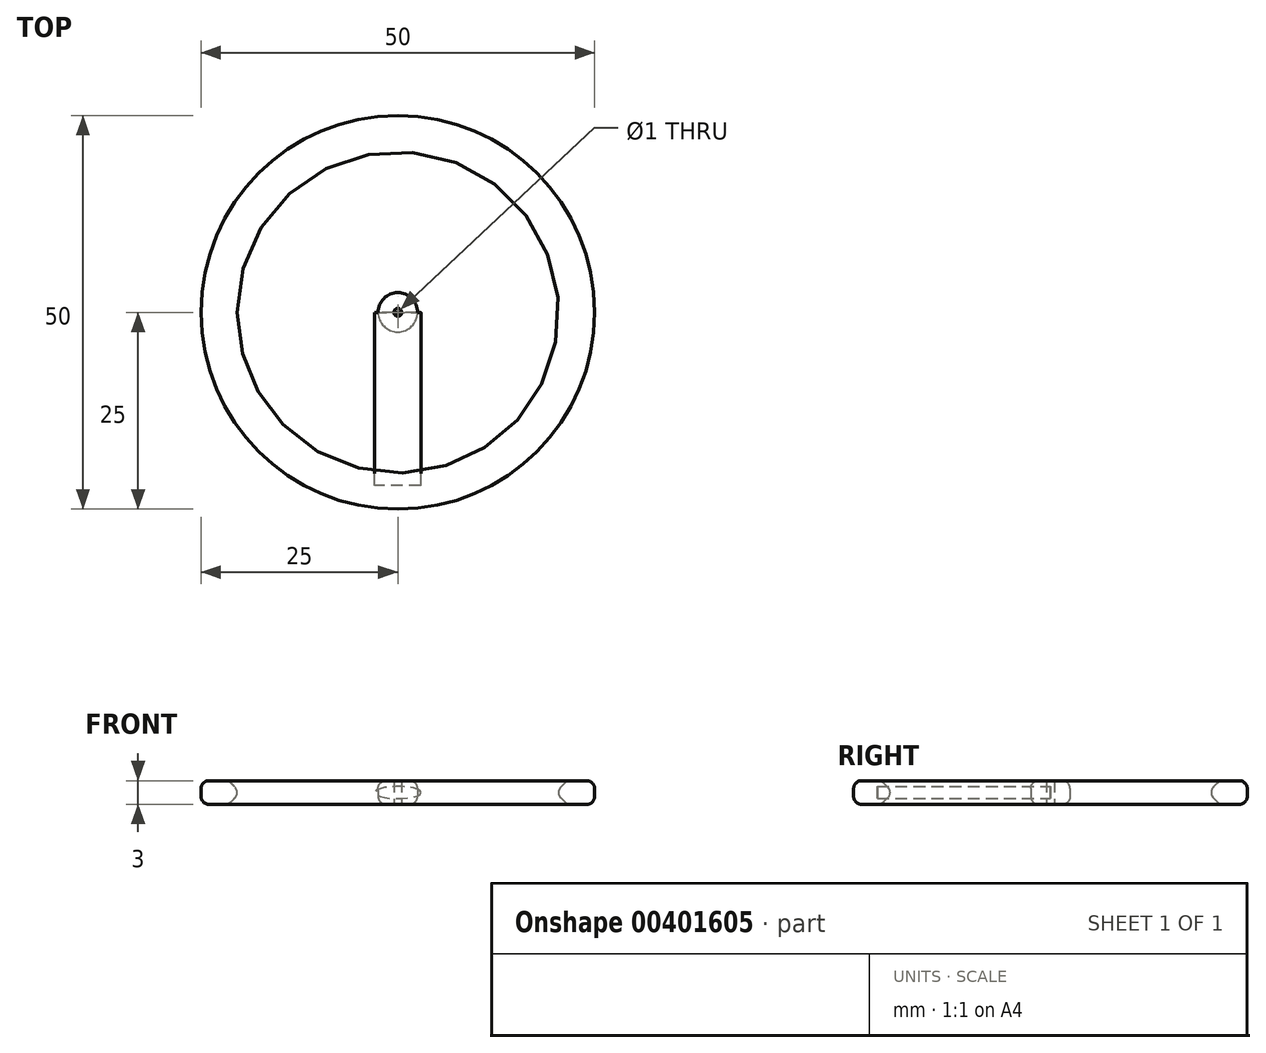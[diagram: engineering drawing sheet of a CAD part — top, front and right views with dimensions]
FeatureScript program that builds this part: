
annotation { "Feature Type Name" : "Feature", "Feature Type Description" : "" }
export const myFeature = defineFeature(function(context is Context, id is Id, definition is map)
    precondition{}
    {
        {
            var Q0;
            Q0=qCreatedBy(makeId("Top.planeOp"),FACE);
            var sketch = newSketch(context, id + "F0", { "sketchPlane" : qUnion([Q0])});
            skCircle(sketch, "E0", {"center": v(0, 0) * mm, "radius": 25 * mm});
            skCircle(sketch, "E1", {"center": v(0, 0) * mm, "radius": 20 * mm});
            skCircle(sketch, "E2", {"center": v(0, 0) * mm, "radius": 2.5 * mm});
            skCircle(sketch, "E3", {"center": v(0, 0) * mm, "radius": 0.5 * mm});
            skSolve(sketch);
        }
        {
            var Q0;
            Q0=makeQuery(id+"F0.imprint","IMPRINT",FACE,{"disambiguationData":[TD([[makeQuery(id+"F0.imprint","IMPRINT",EDGE,{"derivedFrom":sQuery(id+"F0.wireOp",EDGE,"E2")}),1.0]])]});
            var Q1;
            Q1=makeQuery(id+"F0.imprint","IMPRINT",FACE,{"disambiguationData":[TD([[makeQuery(id+"F0.imprint","IMPRINT",EDGE,{"derivedFrom":sQuery(id+"F0.wireOp",EDGE,"E0")}),1.0]])]});
            extrude(context, id + "F1", {"entities" : qUnion([Q0, Q1]), "endBound" : BoundingType.SYMMETRIC, "depth" : 3 * mm});
        }
        {
            var Q0;
            Q0=qCreatedBy(makeId("Front.planeOp"),FACE);
            var sketch = newSketch(context, id + "F2", { "sketchPlane" : qUnion([Q0])});
            skEllipse(sketch, "E4", {"center": v(0, 0) * mm, "majorRadius": 2.93 * mm, "minorRadius": 0.77 * mm, "majorAxis": v(1, 0)});
            skSolve(sketch);
        }
        {
            var Q0;
            Q0 = qSketchRegion(id + "F2", true);
            extrude(context, id + "F3", {"entities" : qUnion([Q0]), "depth" : 22 * mm});
        }
        {
            var Q0;
            Q0=makeQuery(id+"F1.opExtrude","CAP_EDGE",EDGE,{"disambiguationData":[OSD([sQuery(id+"F0.wireOp",EDGE,"E1")])],"isStart":false});
            var Q1;
            Q1=makeQuery(id+"F1.opExtrude","CAP_EDGE",EDGE,{"disambiguationData":[OSD([sQuery(id+"F0.wireOp",EDGE,"E1")])],"isStart":true});
            chamfer(context, id + "F4", {"entities" : qUnion([Q0, Q1]), "width" : 1.5 * mm, "tangentPropagation" : true});
        }
        {
            var Q0;
            {var subQ0=sQuery(id+"F0.wireOp",EDGE,"E1");Q0=makeQuery(id+"F4.opChamfer","BLEND_EDGE",EDGE,{"blendedFrom":[makeQuery(id+"F1.opExtrude","CAP_EDGE",EDGE,{"disambiguationData":[OSD([subQ0])],"isStart":false}),makeQuery(id+"F1.opExtrude","CAP_FACE",FACE,{"disambiguationData":[OSD([sQuery(id+"F0.wireOp",EDGE,"E0"),subQ0])],"isStart":false})],"blendedInto":[makeQuery(id+"F1.opExtrude","CAP_FACE",FACE,{"disambiguationData":[OSD([sQuery(id+"F0.wireOp",EDGE,"E0"),subQ0])],"isStart":false})]});}
            var Q1;
            {var subQ0=sQuery(id+"F0.wireOp",EDGE,"E1");Q1=makeQuery(id+"F4.opChamfer","BLEND_EDGE",EDGE,{"blendedFrom":[makeQuery(id+"F1.opExtrude","CAP_EDGE",EDGE,{"disambiguationData":[OSD([subQ0])],"isStart":true}),makeQuery(id+"F1.opExtrude","CAP_FACE",FACE,{"disambiguationData":[OSD([sQuery(id+"F0.wireOp",EDGE,"E0"),subQ0])],"isStart":true})],"blendedInto":[makeQuery(id+"F1.opExtrude","CAP_FACE",FACE,{"disambiguationData":[OSD([sQuery(id+"F0.wireOp",EDGE,"E0"),subQ0])],"isStart":true})]});}
            var Q2;
            {var subQ0=sQuery(id+"F0.wireOp",EDGE,"E1");Q2=makeQuery(id+"F4.opChamfer","BLEND_EDGE",EDGE,{"blendedFrom":[makeQuery(id+"F1.opExtrude","CAP_EDGE",EDGE,{"disambiguationData":[OSD([subQ0])],"isStart":true}),makeQuery(id+"F1.opExtrude","CAP_EDGE",EDGE,{"disambiguationData":[OSD([subQ0])],"isStart":false})],"blendedInto":[]});}
            var Q3;
            Q3=makeQuery(id+"F1.opExtrude","CAP_EDGE",EDGE,{"disambiguationData":[OSD([sQuery(id+"F0.wireOp",EDGE,"E0")])],"isStart":false});
            var Q4;
            Q4=makeQuery(id+"F1.opExtrude","CAP_EDGE",EDGE,{"disambiguationData":[OSD([sQuery(id+"F0.wireOp",EDGE,"E0")])],"isStart":true});
            var Q5;
            Q5=makeQuery(id+"F1.opExtrude","CAP_EDGE",EDGE,{"disambiguationData":[OSD([sQuery(id+"F0.wireOp",EDGE,"E2")])],"isStart":true});
            var Q6;
            Q6=makeQuery(id+"F1.opExtrude","CAP_EDGE",EDGE,{"disambiguationData":[OSD([sQuery(id+"F0.wireOp",EDGE,"E2")])],"isStart":false});
            fillet(context, id + "F5", {"entities" : qUnion([Q0, Q1, Q2, Q3, Q4, Q5, Q6]), "radius" : 1 * mm, "tangentPropagation" : true, "allowEdgeOverflow" : false});
        }
    });
